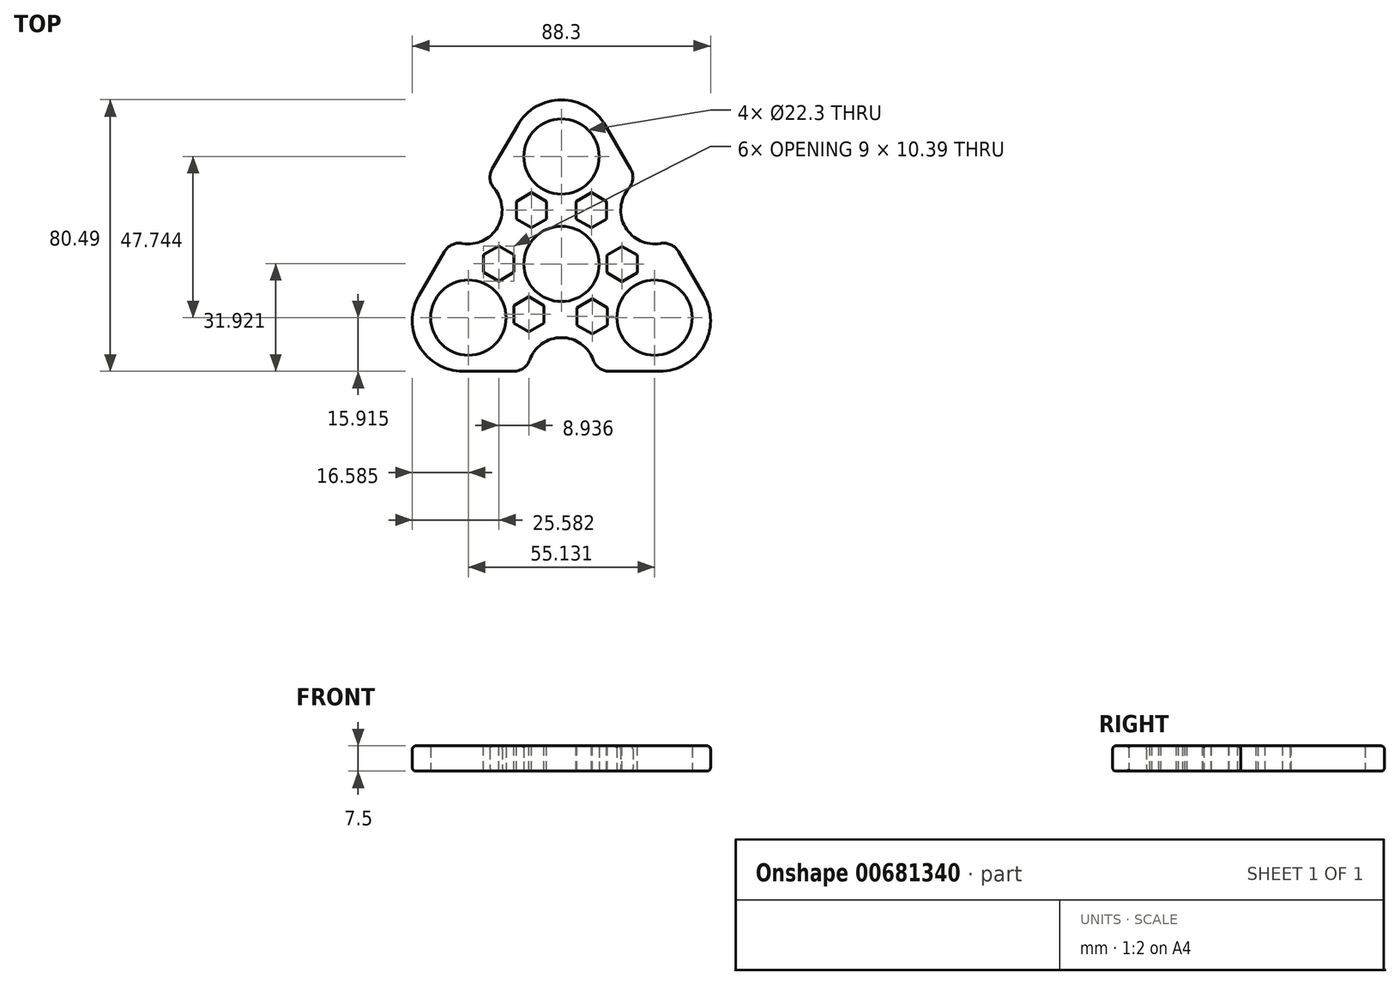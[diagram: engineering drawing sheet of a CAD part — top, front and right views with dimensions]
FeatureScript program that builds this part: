
annotation { "Feature Type Name" : "Feature", "Feature Type Description" : "" }
export const myFeature = defineFeature(function(context is Context, id is Id, definition is map)
    precondition{}
    {
        {
            var Q0;
            Q0=qCreatedBy(makeId("Top.planeOp"),FACE);
            var sketch = newSketch(context, id + "F0", { "sketchPlane" : qUnion([Q0])});
            skCircle(sketch, "E0", {"center": v(0, 0) * mm, "radius": 11.15 * mm});
            skCircle(sketch, "E1.cCircle", {"center": v(0, 0) * mm, "radius": 31.83 * mm, "construction": true});
            skLineSegment(sketch, "E1.0", {"start": v(0, 63.66) * mm, "end": v(55.13, -31.83) * mm});
            skLineSegment(sketch, "E1.1", {"start": v(55.13, -31.83) * mm, "end": v(-55.13, -31.83) * mm});
            skLineSegment(sketch, "E1.2", {"start": v(-55.13, -31.83) * mm, "end": v(0, 63.66) * mm});
            skPoint(sketch, "E1.0.midPoint", {"position": v(27.57, 15.91) * mm});
            skCircle(sketch, "E2", {"center": v(0, 31.83) * mm, "radius": 11.15 * mm});
            skCircle(sketch, "E3", {"center": v(-27.57, -15.91) * mm, "radius": 11.15 * mm});
            skCircle(sketch, "E4", {"center": v(27.57, -15.91) * mm, "radius": 11.15 * mm});
            skCircle(sketch, "E5", {"center": v(-27.57, 15.91) * mm, "radius": 10 * mm});
            skCircle(sketch, "E6", {"center": v(27.57, 15.91) * mm, "radius": 10 * mm});
            skCircle(sketch, "E7", {"center": v(0, -31.83) * mm, "radius": 10 * mm});
            skSolve(sketch);
        }
        {
            var Q0;
            Q0=makeQuery(id+"F0.imprint","IMPRINT",FACE,{"disambiguationData":[TD([[makeQuery(id+"F0.imprint","IMPRINT",EDGE,{"derivedFrom":sQuery(id+"F0.wireOp",EDGE,"E0")}),-1.0]])]});
            extrude(context, id + "F1", {"entities" : qUnion([Q0]), "depth" : 7.5 * mm, "offsetDistance" : 25 * mm});
        }
        {
            var Q0;
            Q0=makeQuery(id+"F1.opExtrude","SWEPT_EDGE",EDGE,{"disambiguationData":[OSD([sQuery(id+"F0.wireOp",EDGE,"E1.0"),sQuery(id+"F0.wireOp",EDGE,"E1.2")])]});
            var Q1;
            Q1=makeQuery(id+"F1.opExtrude","SWEPT_EDGE",EDGE,{"disambiguationData":[OSD([sQuery(id+"F0.wireOp",EDGE,"E1.1"),sQuery(id+"F0.wireOp",EDGE,"E1.2")])]});
            var Q2;
            Q2=makeQuery(id+"F1.opExtrude","SWEPT_EDGE",EDGE,{"disambiguationData":[OSD([sQuery(id+"F0.wireOp",EDGE,"E1.0"),sQuery(id+"F0.wireOp",EDGE,"E1.1")])]});
            fillet(context, id + "F2", {"entities" : qUnion([Q0, Q1, Q2]), "radius" : 15 * mm, "tangentPropagation" : true, "allowEdgeOverflow" : false});
        }
        {
            var Q0;
            Q0=makeQuery(id+"F1.opExtrude","CAP_FACE",FACE,{"disambiguationData":[OSD([sQuery(id+"F0.wireOp",EDGE,"E0"),sQuery(id+"F0.wireOp",EDGE,"E1.0"),sQuery(id+"F0.wireOp",EDGE,"E1.1"),sQuery(id+"F0.wireOp",EDGE,"E1.2"),sQuery(id+"F0.wireOp",EDGE,"E2"),sQuery(id+"F0.wireOp",EDGE,"E3"),sQuery(id+"F0.wireOp",EDGE,"E4"),sQuery(id+"F0.wireOp",EDGE,"2J6Wsjb8-EWeH-ZJ6K-Nj0r-PwiTQXY4kuqp"),sQuery(id+"F0.wireOp",EDGE,"kNyVJvtd-niGE-Z39p-e9RV-1HBrSgLf6Aye"),sQuery(id+"F0.wireOp",EDGE,"6gKmUJXr-A97g-fOzi-Sf8V-XZ0GEmVbGoFn")])],"isStart":false});
            var sketch = newSketch(context, id + "F3", { "sketchPlane" : qUnion([Q0])});
            skPoint(sketch, "E8.startSnap0", {"position": v(0, 15.91) * mm});
            skCircle(sketch, "E9", {"center": v(8.87, 15.91) * mm, "radius": 2.5 * mm});
            skCircle(sketch, "E10", {"center": v(-8.87, 15.91) * mm, "radius": 2.5 * mm});
            skCircle(sketch, "E11", {"center": v(-18.57, 0) * mm, "radius": 2.5 * mm});
            skPoint(sketch, "E11.centerSnap0", {"position": v(-18.57, 0.1) * mm});
            skCircle(sketch, "E12", {"center": v(-9.63, -14.92) * mm, "radius": 2.5 * mm});
            skCircle(sketch, "E13", {"center": v(9.13, -15.57) * mm, "radius": 2.5 * mm});
            skCircle(sketch, "E14", {"center": v(17.94, 0) * mm, "radius": 2.5 * mm});
            skCircle(sketch, "E15.cCircle", {"center": v(-8.87, 15.91) * mm, "radius": 4.5 * mm, "construction": true});
            skLineSegment(sketch, "E15.0", {"start": v(-4.37, 18.51) * mm, "end": v(-4.37, 13.32) * mm});
            skLineSegment(sketch, "E15.1", {"start": v(-4.37, 13.32) * mm, "end": v(-8.87, 10.72) * mm});
            skLineSegment(sketch, "E15.2", {"start": v(-8.87, 10.72) * mm, "end": v(-13.37, 13.32) * mm});
            skLineSegment(sketch, "E15.3", {"start": v(-13.37, 13.32) * mm, "end": v(-13.37, 18.51) * mm});
            skLineSegment(sketch, "E15.4", {"start": v(-13.37, 18.51) * mm, "end": v(-8.87, 21.11) * mm});
            skLineSegment(sketch, "E15.5", {"start": v(-8.87, 21.11) * mm, "end": v(-4.37, 18.51) * mm});
            skPoint(sketch, "E15.0.midPoint", {"position": v(-4.37, 15.91) * mm});
            skCircle(sketch, "E16.cCircle", {"center": v(8.87, 15.91) * mm, "radius": 4.5 * mm, "construction": true});
            skLineSegment(sketch, "E16.0", {"start": v(4.37, 13.32) * mm, "end": v(4.37, 18.51) * mm});
            skLineSegment(sketch, "E16.1", {"start": v(4.37, 18.51) * mm, "end": v(8.87, 21.11) * mm});
            skLineSegment(sketch, "E16.2", {"start": v(8.87, 21.11) * mm, "end": v(13.37, 18.51) * mm});
            skLineSegment(sketch, "E16.3", {"start": v(13.37, 18.51) * mm, "end": v(13.37, 13.32) * mm});
            skLineSegment(sketch, "E16.4", {"start": v(13.37, 13.32) * mm, "end": v(8.87, 10.72) * mm});
            skLineSegment(sketch, "E16.5", {"start": v(8.87, 10.72) * mm, "end": v(4.37, 13.32) * mm});
            skPoint(sketch, "E16.0.midPoint", {"position": v(4.37, 15.91) * mm});
            skCircle(sketch, "E17.cCircle", {"center": v(-18.57, 0.1) * mm, "radius": 4.5 * mm, "construction": true});
            skLineSegment(sketch, "E17.0", {"start": v(-14.07, 2.69) * mm, "end": v(-14.07, -2.5) * mm});
            skLineSegment(sketch, "E17.1", {"start": v(-14.07, -2.5) * mm, "end": v(-18.57, -5.1) * mm});
            skLineSegment(sketch, "E17.2", {"start": v(-18.57, -5.1) * mm, "end": v(-23.07, -2.5) * mm});
            skLineSegment(sketch, "E17.3", {"start": v(-23.07, -2.5) * mm, "end": v(-23.07, 2.69) * mm});
            skLineSegment(sketch, "E17.4", {"start": v(-23.07, 2.69) * mm, "end": v(-18.57, 5.29) * mm});
            skLineSegment(sketch, "E17.5", {"start": v(-18.57, 5.29) * mm, "end": v(-14.07, 2.69) * mm});
            skPoint(sketch, "E17.0.midPoint", {"position": v(-14.07, 0.1) * mm});
            skCircle(sketch, "E18.cCircle", {"center": v(-9.63, -14.92) * mm, "radius": 4.5 * mm, "construction": true});
            skLineSegment(sketch, "E18.0", {"start": v(-9.63, -9.73) * mm, "end": v(-5.13, -12.32) * mm});
            skLineSegment(sketch, "E18.1", {"start": v(-5.13, -12.32) * mm, "end": v(-5.13, -17.52) * mm});
            skLineSegment(sketch, "E18.2", {"start": v(-5.13, -17.52) * mm, "end": v(-9.63, -20.12) * mm});
            skLineSegment(sketch, "E18.3", {"start": v(-9.63, -20.12) * mm, "end": v(-14.13, -17.52) * mm});
            skLineSegment(sketch, "E18.4", {"start": v(-14.13, -17.52) * mm, "end": v(-14.13, -12.32) * mm});
            skLineSegment(sketch, "E18.5", {"start": v(-14.13, -12.32) * mm, "end": v(-9.63, -9.73) * mm});
            skPoint(sketch, "E18.0.midPoint", {"position": v(-7.38, -11.02) * mm});
            skCircle(sketch, "E19.cCircle", {"center": v(9.13, -15.57) * mm, "radius": 4.5 * mm, "construction": true});
            skLineSegment(sketch, "E19.0", {"start": v(13.63, -12.97) * mm, "end": v(13.63, -18.16) * mm});
            skLineSegment(sketch, "E19.1", {"start": v(13.63, -18.16) * mm, "end": v(9.13, -20.76) * mm});
            skLineSegment(sketch, "E19.2", {"start": v(9.13, -20.76) * mm, "end": v(4.63, -18.16) * mm});
            skLineSegment(sketch, "E19.3", {"start": v(4.63, -18.16) * mm, "end": v(4.63, -12.97) * mm});
            skLineSegment(sketch, "E19.4", {"start": v(4.63, -12.97) * mm, "end": v(9.13, -10.37) * mm});
            skLineSegment(sketch, "E19.5", {"start": v(9.13, -10.37) * mm, "end": v(13.63, -12.97) * mm});
            skPoint(sketch, "E19.0.midPoint", {"position": v(13.63, -15.57) * mm});
            skCircle(sketch, "E20.cCircle", {"center": v(17.94, 0) * mm, "radius": 4.5 * mm, "construction": true});
            skLineSegment(sketch, "E20.0", {"start": v(13.44, -2.6) * mm, "end": v(13.44, 2.6) * mm});
            skLineSegment(sketch, "E20.1", {"start": v(13.44, 2.6) * mm, "end": v(17.94, 5.2) * mm});
            skLineSegment(sketch, "E20.2", {"start": v(17.94, 5.2) * mm, "end": v(22.44, 2.6) * mm});
            skLineSegment(sketch, "E20.3", {"start": v(22.44, 2.6) * mm, "end": v(22.44, -2.6) * mm});
            skLineSegment(sketch, "E20.4", {"start": v(22.44, -2.6) * mm, "end": v(17.94, -5.2) * mm});
            skLineSegment(sketch, "E20.5", {"start": v(17.94, -5.2) * mm, "end": v(13.44, -2.6) * mm});
            skPoint(sketch, "E20.0.midPoint", {"position": v(13.44, 0) * mm});
            skSolve(sketch);
        }
        {
            var Q0;
            Q0=makeQuery(id+"F3.imprint","IMPRINT",FACE,{"disambiguationData":[TD([[makeQuery(id+"F3.imprint","IMPRINT",EDGE,{"derivedFrom":sQuery(id+"F3.wireOp",EDGE,"E12")}),-1.0]])]});
            var Q1;
            Q1=makeQuery(id+"F3.imprint","IMPRINT",FACE,{"disambiguationData":[TD([[makeQuery(id+"F3.imprint","IMPRINT",EDGE,{"derivedFrom":sQuery(id+"F3.wireOp",EDGE,"E11")}),-1.0]])]});
            var Q2;
            Q2=makeQuery(id+"F3.imprint","IMPRINT",FACE,{"disambiguationData":[TD([[makeQuery(id+"F3.imprint","IMPRINT",EDGE,{"derivedFrom":sQuery(id+"F3.wireOp",EDGE,"E10")}),-1.0]])]});
            var Q3;
            Q3=makeQuery(id+"F3.imprint","IMPRINT",FACE,{"disambiguationData":[TD([[makeQuery(id+"F3.imprint","IMPRINT",EDGE,{"derivedFrom":sQuery(id+"F3.wireOp",EDGE,"E9")}),-1.0]])]});
            var Q4;
            Q4=makeQuery(id+"F3.imprint","IMPRINT",FACE,{"disambiguationData":[TD([[makeQuery(id+"F3.imprint","IMPRINT",EDGE,{"derivedFrom":sQuery(id+"F3.wireOp",EDGE,"E13")}),-1.0]])]});
            var Q5;
            Q5=makeQuery(id+"F3.imprint","IMPRINT",FACE,{"disambiguationData":[TD([[makeQuery(id+"F3.imprint","IMPRINT",EDGE,{"derivedFrom":sQuery(id+"F3.wireOp",EDGE,"E14")}),-1.0]])]});
            var Q6;
            Q6=makeQuery(id+"F3.imprint","IMPRINT",FACE,{"disambiguationData":[TD([[makeQuery(id+"F3.imprint","IMPRINT",EDGE,{"derivedFrom":sQuery(id+"F3.wireOp",EDGE,"E14")}),1.0]])]});
            var Q7;
            Q7=makeQuery(id+"F3.imprint","IMPRINT",FACE,{"disambiguationData":[TD([[makeQuery(id+"F3.imprint","IMPRINT",EDGE,{"derivedFrom":sQuery(id+"F3.wireOp",EDGE,"E9")}),1.0]])]});
            var Q8;
            Q8=makeQuery(id+"F3.imprint","IMPRINT",FACE,{"disambiguationData":[TD([[makeQuery(id+"F3.imprint","IMPRINT",EDGE,{"derivedFrom":sQuery(id+"F3.wireOp",EDGE,"E10")}),1.0]])]});
            var Q9;
            Q9=makeQuery(id+"F3.imprint","IMPRINT",FACE,{"disambiguationData":[TD([[makeQuery(id+"F3.imprint","IMPRINT",EDGE,{"derivedFrom":sQuery(id+"F3.wireOp",EDGE,"E11")}),1.0]])]});
            var Q10;
            Q10=makeQuery(id+"F3.imprint","IMPRINT",FACE,{"disambiguationData":[TD([[makeQuery(id+"F3.imprint","IMPRINT",EDGE,{"derivedFrom":sQuery(id+"F3.wireOp",EDGE,"E12")}),1.0]])]});
            extrude(context, id + "F4", {"entities" : qUnion([Q0, Q1, Q2, Q3, Q4, Q5, Q6, Q7, Q8, Q9, Q10]), "operationType" : NewBodyOperationType.REMOVE, "endBound" : BoundingType.THROUGH_ALL, "oppositeDirection" : true, "depth" : 25 * mm, "offsetDistance" : 25 * mm});
        }
        {
            var Q0;
            Q0=makeQuery(id+"F4.boolean.opBoolean","SPLIT",FACE,{"disambiguationData":[TD([makeQuery(id+"F4.opExtrude","SWEPT_FACE",FACE,{"disambiguationData":[OSD([sQuery(id+"F3.wireOp",EDGE,"E13")])]})])],"derivedFrom":makeQuery(id+"F1.opExtrude","CAP_FACE",FACE,{"disambiguationData":[OSD([sQuery(id+"F0.wireOp",EDGE,"E0"),sQuery(id+"F0.wireOp",EDGE,"E1.0"),sQuery(id+"F0.wireOp",EDGE,"E1.1"),sQuery(id+"F0.wireOp",EDGE,"E1.2"),sQuery(id+"F0.wireOp",EDGE,"E2"),sQuery(id+"F0.wireOp",EDGE,"E3"),sQuery(id+"F0.wireOp",EDGE,"E4"),sQuery(id+"F0.wireOp",EDGE,"2J6Wsjb8-EWeH-ZJ6K-Nj0r-PwiTQXY4kuqp"),sQuery(id+"F0.wireOp",EDGE,"kNyVJvtd-niGE-Z39p-e9RV-1HBrSgLf6Aye"),sQuery(id+"F0.wireOp",EDGE,"6gKmUJXr-A97g-fOzi-Sf8V-XZ0GEmVbGoFn")])],"isStart":true})});
            extrude(context, id + "F5", {"entities" : qUnion([Q0]), "operationType" : NewBodyOperationType.REMOVE, "endBound" : BoundingType.THROUGH_ALL, "oppositeDirection" : true, "depth" : 25 * mm, "offsetDistance" : 25 * mm});
        }
        {
            var Q0;
            {var subQ0=sQuery(id+"F0.wireOp",EDGE,"E1.2");var subQ1=sQuery(id+"F0.wireOp",EDGE,"E1.0");Q0=makeQuery(id+"F2.opFillet","BLEND_EDGE",EDGE,{"blendedFrom":[makeQuery(id+"F1.opExtrude","SWEPT_EDGE",EDGE,{"disambiguationData":[OSD([subQ1,subQ0])]}),makeQuery(id+"F1.opExtrude","CAP_FACE",FACE,{"disambiguationData":[OSD([sQuery(id+"F0.wireOp",EDGE,"E0"),subQ1,sQuery(id+"F0.wireOp",EDGE,"E1.1"),subQ0,sQuery(id+"F0.wireOp",EDGE,"E2"),sQuery(id+"F0.wireOp",EDGE,"E3"),sQuery(id+"F0.wireOp",EDGE,"E4"),sQuery(id+"F0.wireOp",EDGE,"E5"),sQuery(id+"F0.wireOp",EDGE,"E6"),sQuery(id+"F0.wireOp",EDGE,"E7")])],"isStart":false})],"blendedInto":[makeQuery(id+"F1.opExtrude","CAP_FACE",FACE,{"disambiguationData":[OSD([sQuery(id+"F0.wireOp",EDGE,"E0"),subQ1,sQuery(id+"F0.wireOp",EDGE,"E1.1"),subQ0,sQuery(id+"F0.wireOp",EDGE,"E2"),sQuery(id+"F0.wireOp",EDGE,"E3"),sQuery(id+"F0.wireOp",EDGE,"E4"),sQuery(id+"F0.wireOp",EDGE,"E5"),sQuery(id+"F0.wireOp",EDGE,"E6"),sQuery(id+"F0.wireOp",EDGE,"E7")])],"isStart":false})]});}
            var Q1;
            {var subQ0=sQuery(id+"F0.wireOp",EDGE,"E1.2");Q1=makeQuery(id+"F1.opExtrude","CAP_EDGE",EDGE,{"disambiguationData":[OSD([subQ0]),TDD([makeQuery(id+"F0.imprint","IMPRINT",EDGE,{"disambiguationData":[TD([[makeQuery(id+"F0.imprint","INTERSECT",VERTEX,{"derivedFrom":[sQuery(id+"F0.wireOp",EDGE,"E1.0"),subQ0]}),1.0]])],"derivedFrom":subQ0})])],"isStart":false});}
            var Q2;
            Q2=makeQuery(id+"F1.opExtrude","CAP_EDGE",EDGE,{"disambiguationData":[OSD([sQuery(id+"F0.wireOp",EDGE,"E5")])],"isStart":false});
            var Q3;
            Q3=makeQuery(id+"F1.opExtrude","CAP_EDGE",EDGE,{"disambiguationData":[OSD([sQuery(id+"F0.wireOp",EDGE,"E6")])],"isStart":false});
            var Q4;
            {var subQ0=sQuery(id+"F0.wireOp",EDGE,"E1.0");Q4=makeQuery(id+"F1.opExtrude","CAP_EDGE",EDGE,{"disambiguationData":[OSD([subQ0]),TDD([makeQuery(id+"F0.imprint","IMPRINT",EDGE,{"disambiguationData":[TD([[makeQuery(id+"F0.imprint","INTERSECT",VERTEX,{"derivedFrom":[subQ0,sQuery(id+"F0.wireOp",EDGE,"E1.1")]}),1.0]])],"derivedFrom":subQ0})])],"isStart":false});}
            var Q5;
            Q5=makeQuery(id+"F1.opExtrude","CAP_EDGE",EDGE,{"disambiguationData":[OSD([sQuery(id+"F0.wireOp",EDGE,"E7")])],"isStart":false});
            var Q6;
            {var subQ0=sQuery(id+"F0.wireOp",EDGE,"E1.2");var subQ1=sQuery(id+"F0.wireOp",EDGE,"E1.1");Q6=makeQuery(id+"F2.opFillet","BLEND_EDGE",EDGE,{"blendedFrom":[makeQuery(id+"F1.opExtrude","SWEPT_EDGE",EDGE,{"disambiguationData":[OSD([subQ1,subQ0])]}),makeQuery(id+"F1.opExtrude","CAP_FACE",FACE,{"disambiguationData":[OSD([sQuery(id+"F0.wireOp",EDGE,"E0"),sQuery(id+"F0.wireOp",EDGE,"E1.0"),subQ1,subQ0,sQuery(id+"F0.wireOp",EDGE,"E2"),sQuery(id+"F0.wireOp",EDGE,"E3"),sQuery(id+"F0.wireOp",EDGE,"E4"),sQuery(id+"F0.wireOp",EDGE,"E5"),sQuery(id+"F0.wireOp",EDGE,"E6"),sQuery(id+"F0.wireOp",EDGE,"E7")])],"isStart":false})],"blendedInto":[makeQuery(id+"F1.opExtrude","CAP_FACE",FACE,{"disambiguationData":[OSD([sQuery(id+"F0.wireOp",EDGE,"E0"),sQuery(id+"F0.wireOp",EDGE,"E1.0"),subQ1,subQ0,sQuery(id+"F0.wireOp",EDGE,"E2"),sQuery(id+"F0.wireOp",EDGE,"E3"),sQuery(id+"F0.wireOp",EDGE,"E4"),sQuery(id+"F0.wireOp",EDGE,"E5"),sQuery(id+"F0.wireOp",EDGE,"E6"),sQuery(id+"F0.wireOp",EDGE,"E7")])],"isStart":false})]});}
            var Q7;
            {var subQ0=sQuery(id+"F0.wireOp",EDGE,"E1.0");Q7=makeQuery(id+"F1.opExtrude","CAP_EDGE",EDGE,{"disambiguationData":[OSD([subQ0]),TDD([makeQuery(id+"F0.imprint","IMPRINT",EDGE,{"disambiguationData":[TD([[makeQuery(id+"F0.imprint","INTERSECT",VERTEX,{"derivedFrom":[subQ0,sQuery(id+"F0.wireOp",EDGE,"E1.2")]}),-1.0]])],"derivedFrom":subQ0})])],"isStart":true});}
            var Q8;
            Q8=makeQuery(id+"F1.opExtrude","CAP_EDGE",EDGE,{"disambiguationData":[OSD([sQuery(id+"F0.wireOp",EDGE,"E6")])],"isStart":true});
            var Q9;
            {var subQ0=sQuery(id+"F0.wireOp",EDGE,"E1.1");var subQ1=sQuery(id+"F0.wireOp",EDGE,"E1.0");Q9=makeQuery(id+"F2.opFillet","BLEND_EDGE",EDGE,{"blendedFrom":[makeQuery(id+"F1.opExtrude","SWEPT_EDGE",EDGE,{"disambiguationData":[OSD([subQ1,subQ0])]}),makeQuery(id+"F1.opExtrude","CAP_FACE",FACE,{"disambiguationData":[OSD([sQuery(id+"F0.wireOp",EDGE,"E0"),subQ1,subQ0,sQuery(id+"F0.wireOp",EDGE,"E1.2"),sQuery(id+"F0.wireOp",EDGE,"E2"),sQuery(id+"F0.wireOp",EDGE,"E3"),sQuery(id+"F0.wireOp",EDGE,"E4"),sQuery(id+"F0.wireOp",EDGE,"E5"),sQuery(id+"F0.wireOp",EDGE,"E6"),sQuery(id+"F0.wireOp",EDGE,"E7")])],"isStart":true})],"blendedInto":[makeQuery(id+"F1.opExtrude","CAP_FACE",FACE,{"disambiguationData":[OSD([sQuery(id+"F0.wireOp",EDGE,"E0"),subQ1,subQ0,sQuery(id+"F0.wireOp",EDGE,"E1.2"),sQuery(id+"F0.wireOp",EDGE,"E2"),sQuery(id+"F0.wireOp",EDGE,"E3"),sQuery(id+"F0.wireOp",EDGE,"E4"),sQuery(id+"F0.wireOp",EDGE,"E5"),sQuery(id+"F0.wireOp",EDGE,"E6"),sQuery(id+"F0.wireOp",EDGE,"E7")])],"isStart":true})]});}
            var Q10;
            {var subQ0=sQuery(id+"F0.wireOp",EDGE,"E1.1");Q10=makeQuery(id+"F1.opExtrude","CAP_EDGE",EDGE,{"disambiguationData":[OSD([subQ0]),TDD([makeQuery(id+"F0.imprint","IMPRINT",EDGE,{"disambiguationData":[TD([[makeQuery(id+"F0.imprint","INTERSECT",VERTEX,{"derivedFrom":[sQuery(id+"F0.wireOp",EDGE,"E1.0"),subQ0]}),-1.0]])],"derivedFrom":subQ0})])],"isStart":true});}
            var Q11;
            {var subQ0=sQuery(id+"F0.wireOp",EDGE,"E1.2");Q11=makeQuery(id+"F1.opExtrude","CAP_EDGE",EDGE,{"disambiguationData":[OSD([subQ0]),TDD([makeQuery(id+"F0.imprint","IMPRINT",EDGE,{"disambiguationData":[TD([[makeQuery(id+"F0.imprint","INTERSECT",VERTEX,{"derivedFrom":[sQuery(id+"F0.wireOp",EDGE,"E1.1"),subQ0]}),-1.0]])],"derivedFrom":subQ0})])],"isStart":true});}
            var Q12;
            {var subQ0=sQuery(id+"F0.wireOp",EDGE,"E1.1");Q12=makeQuery(id+"F1.opExtrude","CAP_EDGE",EDGE,{"disambiguationData":[OSD([subQ0]),TDD([makeQuery(id+"F0.imprint","IMPRINT",EDGE,{"disambiguationData":[TD([[makeQuery(id+"F0.imprint","INTERSECT",VERTEX,{"derivedFrom":[subQ0,sQuery(id+"F0.wireOp",EDGE,"E1.2")]}),1.0]])],"derivedFrom":subQ0})])],"isStart":true});}
            var Q13;
            {var subQ0=sQuery(id+"F0.wireOp",EDGE,"E1.2");Q13=makeQuery(id+"F1.opExtrude","CAP_EDGE",EDGE,{"disambiguationData":[OSD([subQ0]),TDD([makeQuery(id+"F0.imprint","IMPRINT",EDGE,{"disambiguationData":[TD([[makeQuery(id+"F0.imprint","INTERSECT",VERTEX,{"derivedFrom":[sQuery(id+"F0.wireOp",EDGE,"E1.0"),subQ0]}),1.0]])],"derivedFrom":subQ0})])],"isStart":true});}
            var Q14;
            Q14=makeQuery(id+"F1.opExtrude","CAP_EDGE",EDGE,{"disambiguationData":[OSD([sQuery(id+"F0.wireOp",EDGE,"E5")])],"isStart":true});
            var Q15;
            Q15=makeQuery(id+"F1.opExtrude","CAP_EDGE",EDGE,{"disambiguationData":[OSD([sQuery(id+"F0.wireOp",EDGE,"E7")])],"isStart":true});
            fillet(context, id + "F6", {"entities" : qUnion([Q0, Q1, Q2, Q3, Q4, Q5, Q6, Q7, Q8, Q9, Q10, Q11, Q12, Q13, Q14, Q15]), "radius" : 1 * mm, "tangentPropagation" : true, "allowEdgeOverflow" : false});
        }
        {
            var Q0;
            Q0=makeQuery(id+"F1.opExtrude","CAP_EDGE",EDGE,{"disambiguationData":[OSD([sQuery(id+"F0.wireOp",EDGE,"E2")])],"isStart":false});
            var Q1;
            Q1=makeQuery(id+"F1.opExtrude","CAP_EDGE",EDGE,{"disambiguationData":[OSD([sQuery(id+"F0.wireOp",EDGE,"E3")])],"isStart":false});
            var Q2;
            Q2=makeQuery(id+"F1.opExtrude","CAP_EDGE",EDGE,{"disambiguationData":[OSD([sQuery(id+"F0.wireOp",EDGE,"E4")])],"isStart":false});
            var Q3;
            Q3=makeQuery(id+"F1.opExtrude","CAP_EDGE",EDGE,{"disambiguationData":[OSD([sQuery(id+"F0.wireOp",EDGE,"E2")])],"isStart":true});
            var Q4;
            Q4=makeQuery(id+"F1.opExtrude","CAP_EDGE",EDGE,{"disambiguationData":[OSD([sQuery(id+"F0.wireOp",EDGE,"E4")])],"isStart":true});
            var Q5;
            Q5=makeQuery(id+"F1.opExtrude","CAP_EDGE",EDGE,{"disambiguationData":[OSD([sQuery(id+"F0.wireOp",EDGE,"E3")])],"isStart":true});
            fillet(context, id + "F7", {"entities" : qUnion([Q0, Q1, Q2, Q3, Q4, Q5]), "radius" : 0.5 * mm, "tangentPropagation" : true, "allowEdgeOverflow" : false});
        }
        {
            var Q0;
            {var subQ0=sQuery(id+"F0.wireOp",EDGE,"E6");var subQ1=sQuery(id+"F0.wireOp",EDGE,"E1.0");Q0=makeQuery(id+"F1.opExtrude","SWEPT_EDGE",EDGE,{"disambiguationData":[OSD([subQ1,subQ0]),TDD([makeQuery(id+"F0.imprint","INTERSECT",VERTEX,{"disambiguationData":[OD(1.0)],"derivedFrom":[subQ1,subQ0]})])]});}
            var Q1;
            {var subQ0=sQuery(id+"F0.wireOp",EDGE,"E6");var subQ1=sQuery(id+"F0.wireOp",EDGE,"E1.0");Q1=makeQuery(id+"F1.opExtrude","SWEPT_EDGE",EDGE,{"disambiguationData":[OSD([subQ1,subQ0]),TDD([makeQuery(id+"F0.imprint","INTERSECT",VERTEX,{"disambiguationData":[OD(0.0)],"derivedFrom":[subQ1,subQ0]})])]});}
            var Q2;
            {var subQ0=sQuery(id+"F0.wireOp",EDGE,"E7");var subQ1=sQuery(id+"F0.wireOp",EDGE,"E1.1");Q2=makeQuery(id+"F1.opExtrude","SWEPT_EDGE",EDGE,{"disambiguationData":[OSD([subQ1,subQ0]),TDD([makeQuery(id+"F0.imprint","INTERSECT",VERTEX,{"disambiguationData":[OD(1.0)],"derivedFrom":[subQ1,subQ0]})])]});}
            var Q3;
            {var subQ0=sQuery(id+"F0.wireOp",EDGE,"E5");var subQ1=sQuery(id+"F0.wireOp",EDGE,"E1.2");Q3=makeQuery(id+"F1.opExtrude","SWEPT_EDGE",EDGE,{"disambiguationData":[OSD([subQ1,subQ0]),TDD([makeQuery(id+"F0.imprint","INTERSECT",VERTEX,{"disambiguationData":[OD(0.0)],"derivedFrom":[subQ1,subQ0]})])]});}
            var Q4;
            {var subQ0=sQuery(id+"F0.wireOp",EDGE,"E5");var subQ1=sQuery(id+"F0.wireOp",EDGE,"E1.2");Q4=makeQuery(id+"F1.opExtrude","SWEPT_EDGE",EDGE,{"disambiguationData":[OSD([subQ1,subQ0]),TDD([makeQuery(id+"F0.imprint","INTERSECT",VERTEX,{"disambiguationData":[OD(1.0)],"derivedFrom":[subQ1,subQ0]})])]});}
            var Q5;
            {var subQ0=sQuery(id+"F0.wireOp",EDGE,"E7");var subQ1=sQuery(id+"F0.wireOp",EDGE,"E1.1");Q5=makeQuery(id+"F1.opExtrude","SWEPT_EDGE",EDGE,{"disambiguationData":[OSD([subQ1,subQ0]),TDD([makeQuery(id+"F0.imprint","INTERSECT",VERTEX,{"disambiguationData":[OD(0.0)],"derivedFrom":[subQ1,subQ0]})])]});}
            fillet(context, id + "F8", {"entities" : qUnion([Q0, Q1, Q2, Q3, Q4, Q5]), "radius" : 5 * mm, "tangentPropagation" : true, "allowEdgeOverflow" : false});
        }
    });
